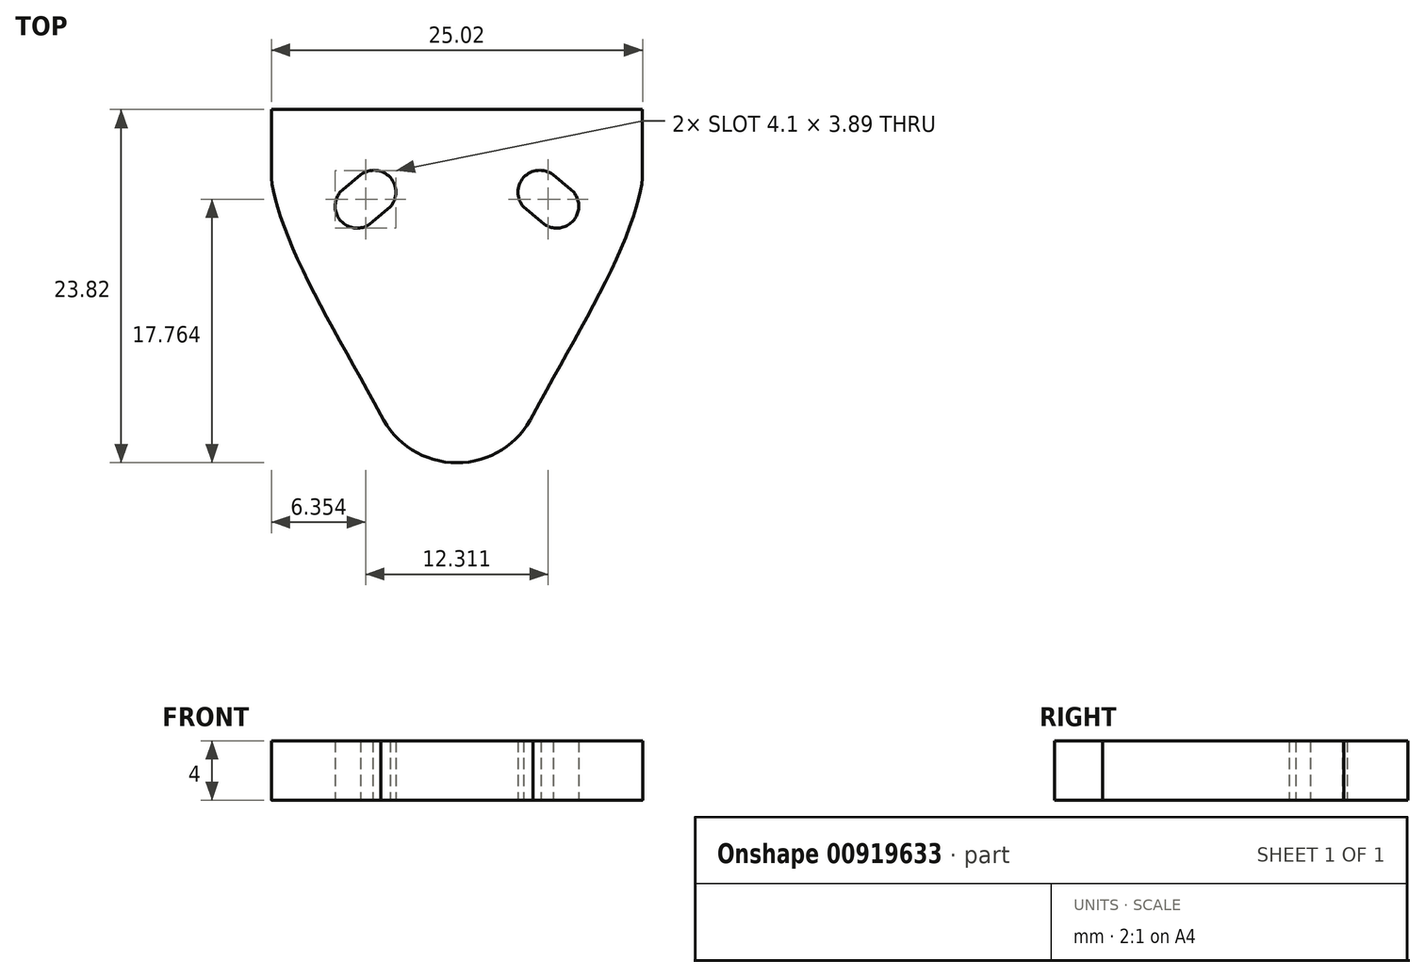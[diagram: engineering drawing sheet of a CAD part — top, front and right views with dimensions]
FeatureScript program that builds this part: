
annotation { "Feature Type Name" : "Feature", "Feature Type Description" : "" }
export const myFeature = defineFeature(function(context is Context, id is Id, definition is map)
    precondition{}
    {
        {
            var Q0;
            Q0=qCreatedBy(makeId("Top.planeOp"),FACE);
            var sketch = newSketch(context, id + "F0", { "sketchPlane" : qUnion([Q0])});
            skArc(sketch, "E0", {"start": v(-5.15, -20.56) * mm, "mid": v(-3.05, -22.94) * mm, "end": v(0, -23.82) * mm});
            skLineSegment(sketch, "E1.bottom", {"start": v(0, 0) * mm, "end": v(-12.5, 0) * mm});
            skLineSegment(sketch, "E1.right", {"start": v(-12.5, 0) * mm, "end": v(-12.5, -4.33) * mm});
            skPoint(sketch, "E1.middle", {"position": v(0, 0) * mm});
            skFitSpline(sketch, "E2", {"points": [v(-12.5, -4.33) * mm, v(-11.08, -9.31) * mm, v(-5.13, -20.6) * mm, v(-5.15, -20.56) * mm], "startDerivative": vector(-0.72, -6.32) * mm, "endDerivative": vector(-22.78, 42.97) * mm});
            skLineSegment(sketch, "E3", {"start": v(0, 0) * mm, "end": v(0, -23.82) * mm});
            skArc(sketch, "E4", {"start": v(-4.5, -6.58) * mm, "mid": v(-4.5, -4.58) * mm, "end": v(-6.49, -4.41) * mm});
            skArc(sketch, "E5", {"start": v(-7.67, -5.38) * mm, "mid": v(-7.82, -7.53) * mm, "end": v(-5.67, -7.55) * mm});
            skLineSegment(sketch, "E6", {"start": v(-6.49, -4.41) * mm, "end": v(-7.67, -5.38) * mm});
            skLineSegment(sketch, "E7", {"start": v(-5.67, -7.55) * mm, "end": v(-4.5, -6.58) * mm});
            skSolve(sketch);
        }
        {
            var Q0;
            Q0 = qSketchRegion(id + "F0", true);
            extrude(context, id + "F1", {"entities" : qUnion([Q0]), "depth" : 4 * mm, "offsetDistance" : 25 * mm});
        }
        {
            var Q0;
            Q0=makeQuery(id+"F1.opExtrude","SWEPT_BODY",BODY,{"disambiguationData":[OSD([sQuery(id+"F0.wireOp",EDGE,"E0"),sQuery(id+"F0.wireOp",EDGE,"E1.bottom"),sQuery(id+"F0.wireOp",EDGE,"E1.right"),sQuery(id+"F0.wireOp",EDGE,"E2"),sQuery(id+"F0.wireOp",EDGE,"E3"),sQuery(id+"F0.wireOp",EDGE,"E4"),sQuery(id+"F0.wireOp",EDGE,"E5"),sQuery(id+"F0.wireOp",EDGE,"E6"),sQuery(id+"F0.wireOp",EDGE,"E7")])]});
            var Q1;
            Q1=qCreatedBy(makeId("Right.planeOp"),FACE);
            mirror(context, id + "F2", {"operationType" : NewBodyOperationType.ADD, "entities" : qUnion([Q0]), "mirrorPlane" : qUnion([Q1])});
        }
    });
